# Revit family: REC-PAR2001208R
name_source: partatom
category: Structural Connections
units: mm (PartAtom-declared; Revit-internal decimal feet)

## family parameters
Cut with Voids When Loaded = Yes
Enable Cutting in Views = Yes
Host = Face
Material for Model Behavior = Steel
Shared = No

## types (1)
- PAR2001208R
    Classification.Uniclass.Pr.Description = Brackets
    Classification.Uniclass.Pr.Number = Pr_20_85_09
    Cost = 0 $
    Creado por: = Deliprogal SL
    Default Elevation = 0 mm  [stored 0 ft]
    Description = Angle plate reinforced 200x120x80x8 mm, slotted hole 17x64 mm on one side and 2 holes Ø17 mm on another side.
    Description_ESP = Pletina angular reforzada 200x120x80x8 mm, coliso 17x64 mm en una ala y 2 TØ17mm en la otra.
    Export Type to IFC As = IfcElementAssembly
    Fecha Ultima Revision: = 01/03/2024
    Fecha de Creacion: = 01/03/2024
    IFCExportAs = IfcElementAssembly
    IFCExportType = Brackets
    Keynote = Anti-tilt anchor for fixing panels to concrete structures by means of interposing profiles, anchor bolts or threaded sleeves.
    Keynote_ESP = Anclaje antivuelco para fijación de paneles a estructura de hormigón mediante la interposición de perfiles, tornillos de anclaje o casquillos roscados.
    Manufacturer = RECENSE
    Model = PAR2001208R
    Type IFC Predefined Type = Brackets
    URL = https://recense.com
    Visible = Yes

note: [stored X ft] marks values corroborated as IEEE doubles in the binary element streams (Revit-internal decimal feet)

## geometry (parser evidence)
native form markers: Sweep x3
no freeform markers — native parametric forms only
